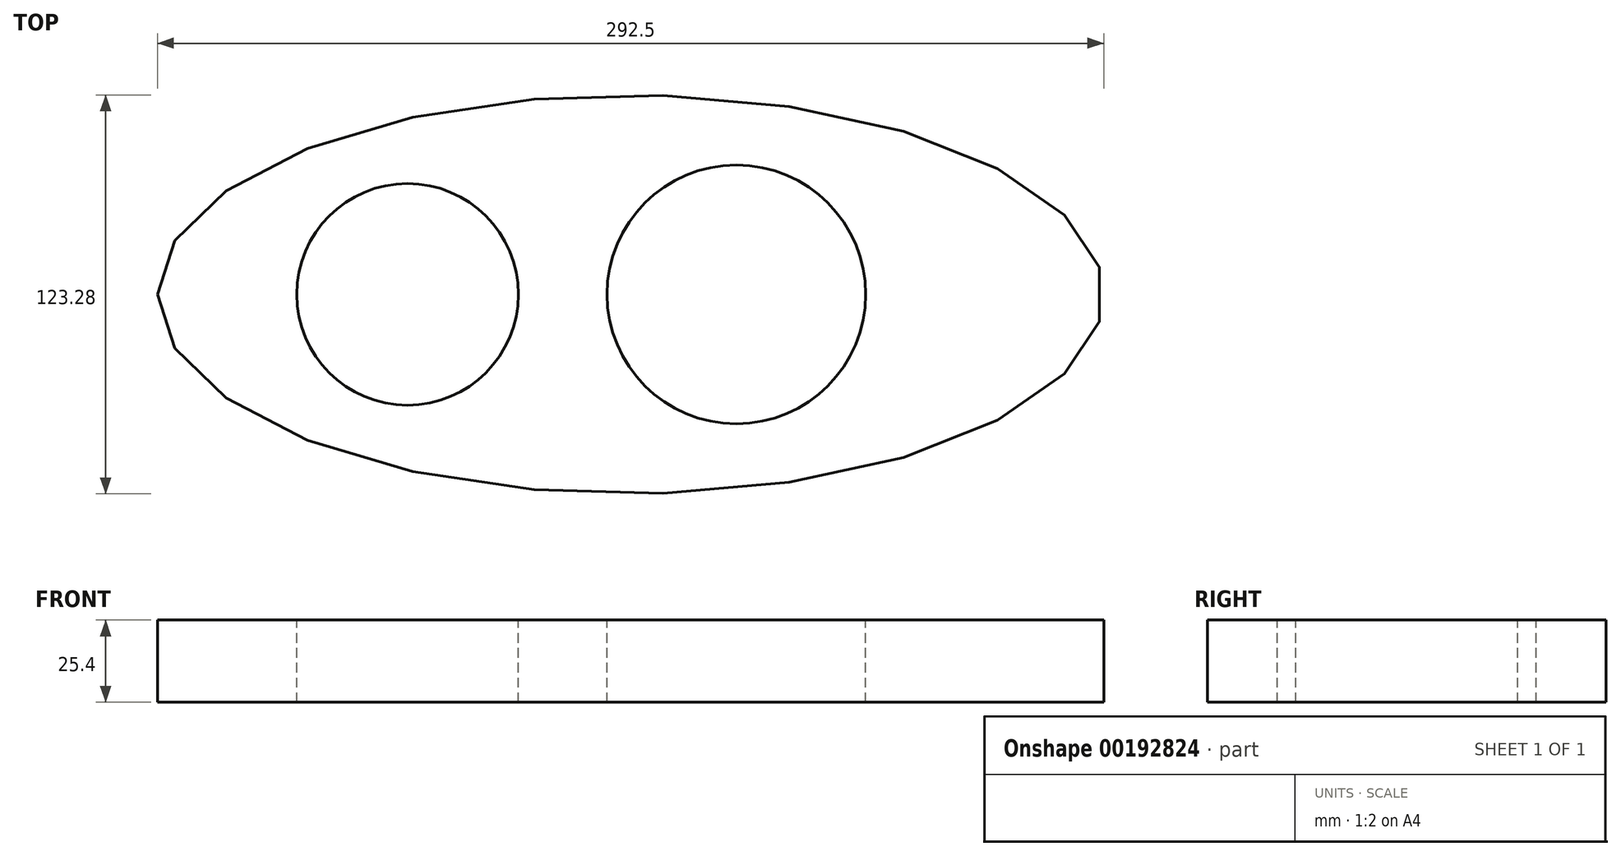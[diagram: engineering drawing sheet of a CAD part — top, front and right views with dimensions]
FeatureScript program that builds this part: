
annotation { "Feature Type Name" : "Feature", "Feature Type Description" : "" }
export const myFeature = defineFeature(function(context is Context, id is Id, definition is map)
    precondition{}
    {
        {
            var Q0;
            Q0=qCreatedBy(makeId("Top.planeOp"),FACE);
            var sketch = newSketch(context, id + "F0", { "sketchPlane" : qUnion([Q0])});
            skCircle(sketch, "E0", {"center": v(-68.93, 0) * mm, "radius": 34.25 * mm});
            skCircle(sketch, "E1", {"center": v(32.7, 0) * mm, "radius": 39.98 * mm});
            skEllipse(sketch, "E2", {"center": v(0, 0) * mm, "majorRadius": 146.25 * mm, "minorRadius": 61.64 * mm, "majorAxis": v(-1, 0)});
            skSolve(sketch);
        }
        {
            var Q0;
            Q0=makeQuery(id+"F0.imprint","IMPRINT",FACE,{"disambiguationData":[TD([[makeQuery(id+"F0.imprint","IMPRINT",EDGE,{"derivedFrom":sQuery(id+"F0.wireOp",EDGE,"E0")}),-1.0]])]});
            var Q1;
            Q1=sQuery(id+"F0.wireOp",EDGE,"E2");
            var Q2;
            Q2=sQuery(id+"F0.wireOp",EDGE,"E0");
            var Q3;
            Q3=sQuery(id+"F0.wireOp",EDGE,"E1");
            extrude(context, id + "F1", {"entities" : qUnion([Q0]), "bodyType" : ToolBodyType.SURFACE, "surfaceEntities" : qUnion([Q1, Q2, Q3]), "depth" : 25.4 * mm});
        }
    });
